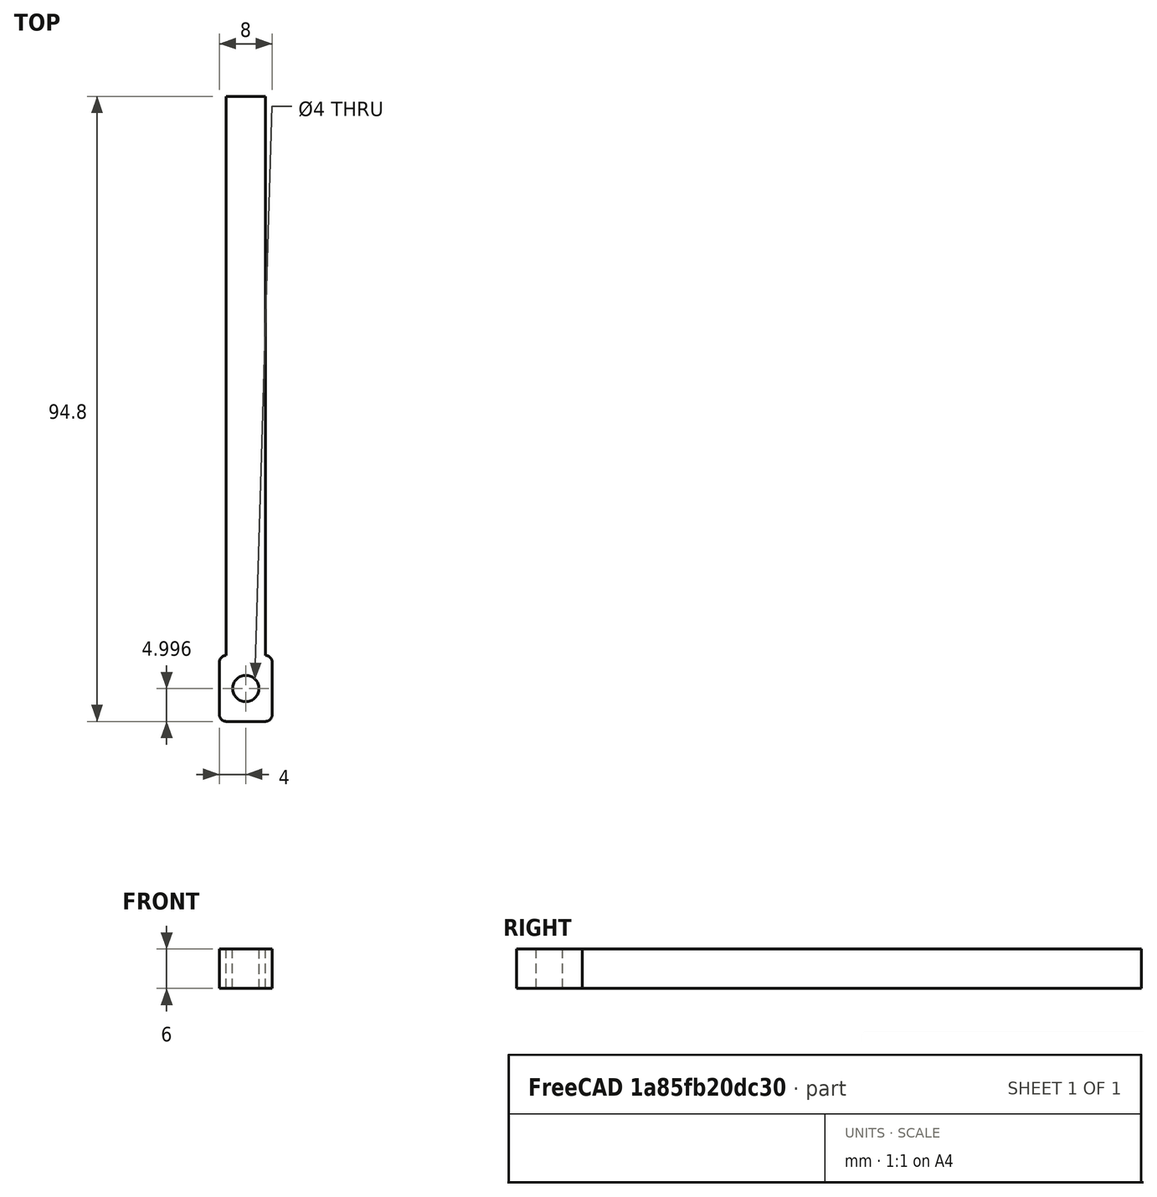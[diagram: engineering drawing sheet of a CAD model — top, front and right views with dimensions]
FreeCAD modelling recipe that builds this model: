
FCSTD DOCUMENT  (FreeCAD 0.18.1R)
Label: shub5R
License: All rights reserved
LicenseURL: http://en.wikipedia.org/wiki/All_rights_reserved
objects: TechDraw::DrawViewDimension×8, TechDraw::DrawProjGroupItem×4, Sketcher::SketchObject×3, PartDesign::Pocket×2, PartDesign::Pad×1, PartDesign::Body×1, TechDraw::DrawSVGTemplate×1, TechDraw::DrawProjGroup×1, TechDraw::DrawPage×1
note: 10 computed .brp shape members not serialized (recipe doc carries the construction recipe); baked Part::Feature solids carry a one-line shape summary decoded from their .brp

FEATURE [Sketcher::SketchObject] Sketch
  MapMode = 5
  Support = -> [XY_Plane]
  sketch-geometry (8):
    g0: LineSegment StartX=1 StartY=94.8 StartZ=0 EndX=7 EndY=94.8 EndZ=0
    g1: LineSegment StartX=7 StartY=94.8 StartZ=0 EndX=7 EndY=10 EndZ=0
    g2: LineSegment StartX=7 StartY=10 StartZ=0 EndX=8 EndY=10 EndZ=0
    g3: LineSegment StartX=8 StartY=10 StartZ=0 EndX=8 EndY=0 EndZ=0
    g4: LineSegment StartX=8 StartY=0 StartZ=0 EndX=0 EndY=0 EndZ=0
    g5: LineSegment StartX=0 StartY=0 StartZ=0 EndX=0 EndY=10 EndZ=0
    g6: LineSegment StartX=0 StartY=10 StartZ=0 EndX=1 EndY=10 EndZ=0
    g7: LineSegment StartX=1 StartY=10 StartZ=0 EndX=1 EndY=94.8 EndZ=0
  constraints (23):
    c: Coincident(g0,g1)
    c: Coincident(g1,g2)
    c: Coincident(g2,g3)
    c: Coincident(g3,g4)
    c: Coincident(g4,g5)
    c: Coincident(g5,g6)
    c: Coincident(g6,g7)
    c: Coincident(g7,g0)
    c: Vertical(g7)
    c: Horizontal(g0)
    c: DistanceY(g7,g7) = 84.8
    c: Horizontal(g6)
    c: DistanceY(g1,g1) = 84.8
    c: Horizontal(g2)
    c: Vertical(g1)
    c: DistanceX(g0,g0) = 6
    c: Vertical(g5)
    c: Vertical(g3)
    c: Horizontal(g4)
    c: DistanceY(g5,g5) = 10
    c: DistanceX(g4,g4) = 8
    c: DistanceX(g6,g6) = 1
    c: Coincident(g4,g-1)
FEATURE [PartDesign::Pad] Pad
  Length = 6
  Length2 = 100
  Profile = -> Sketch
  Type = 0
FEATURE [Sketcher::SketchObject] Sketch001
  ExternalGeometry = -> [Pad]
  MapMode = 5
  Placement = pos=(0,0,6) rot=(0,0,1;0rad)
  Support = -> [Pad]
  sketch-geometry (1):
    g0: Circle CenterX=4 CenterY=4.996 CenterZ=0 NormalX=0 NormalY=0 NormalZ=1 AngleXU=0 Radius=2
  constraints (3):
    c: Radius(g0) = 2
    c: Distance(g-1,g0) = 6.4
    c: Distance(g0,g-3) = 4
FEATURE [PartDesign::Pocket] Pocket
  BaseFeature = -> Pad
  Length = 8
  Length2 = 100
  Profile = -> Sketch001
  Type = 0
FEATURE [Sketcher::SketchObject] Sketch002
  ExternalGeometry = -> [Pocket]
  MapMode = 5
  Placement = pos=(0,0,6) rot=(0,0,1;0rad)
  Support = -> [Pocket]
  sketch-geometry (12):
    g0: ArcOfCircle CenterX=1 CenterY=1 CenterZ=0 NormalX=0 NormalY=0 NormalZ=1 AngleXU=0 Radius=1 StartAngle=3.14159 EndAngle=4.71239
    g1: ArcOfCircle CenterX=1 CenterY=9 CenterZ=0 NormalX=0 NormalY=0 NormalZ=1 AngleXU=0 Radius=1 StartAngle=1.5708 EndAngle=3.14159
    g2: ArcOfCircle CenterX=7 CenterY=9 CenterZ=0 NormalX=0 NormalY=0 NormalZ=1 AngleXU=0 Radius=1 StartAngle=1.3777e-12 EndAngle=1.5708
    g3: ArcOfCircle CenterX=7 CenterY=1 CenterZ=0 NormalX=0 NormalY=0 NormalZ=1 AngleXU=0 Radius=1 StartAngle=4.71239 EndAngle=6.28319
    g4: LineSegment StartX=0 StartY=9 StartZ=0 EndX=0 EndY=10 EndZ=0
    g5: LineSegment StartX=0 StartY=10 StartZ=0 EndX=1 EndY=10 EndZ=0
    g6: LineSegment StartX=0 StartY=1 StartZ=0 EndX=0 EndY=0 EndZ=0
    g7: LineSegment StartX=0 StartY=0 StartZ=0 EndX=1 EndY=0 EndZ=0
    g8: LineSegment StartX=7 StartY=0 StartZ=0 EndX=8 EndY=0 EndZ=0
    g9: LineSegment StartX=8 StartY=0 StartZ=0 EndX=8 EndY=1 EndZ=0
    g10: LineSegment StartX=7 StartY=10 StartZ=0 EndX=8 EndY=10 EndZ=0
    g11: LineSegment StartX=8 StartY=10 StartZ=0 EndX=8 EndY=9 EndZ=0
  constraints (37):
    c: Coincident(g1,g-5)
    c: Angle(g1) = 1.5708
    c: Angle(g2) = 1.5708
    c: Radius(g2) = 1
    c: Radius(g3) = 1
    c: Coincident(g4,g5)
    c: Coincident(g6,g7)
    c: Coincident(g8,g9)
    c: Coincident(g10,g11)
    c: Vertical(g4)
    c: Coincident(g4,g1)
    c: Coincident(g1,g5)
    c: Horizontal(g5)
    c: Radius(g1) = 1
    c: DistanceX(g5,g5) = 1
    c: Coincident(g0,g6)
    c: Coincident(g0,g7)
    c: Horizontal(g7)
    c: Vertical(g6)
    c: Radius(g0) = 1
    c: DistanceX(g7,g7) = 1
    c: Coincident(g6,g-1)
    c: Coincident(g9,g3)
    c: Coincident(g8,g-7)
    c: Angle(g3) = 1.5708
    c: DistanceY(g9,g9) = 1
    c: Coincident(g3,g8)
    c: Vertical(g9)
    c: Horizontal(g8)
    c: Coincident(g10,g-7)
    c: Vertical(g11)
    c: Horizontal(g10)
    c: DistanceY(g11,g11) = 1
    c: Distance(g2,g3) = 8
    c: Distance(g1,g0) = 8
    c: Distance(g1,g2) = 6
    c: Coincident(g2,g10)
FEATURE [PartDesign::Pocket] Pocket001
  BaseFeature = -> Pocket
  Length = 7
  Length2 = 100
  Profile = -> Sketch002
  Type = 0
FEATURE [PartDesign::Body] Body
  Group = -> [Sketch,Pad,Sketch001,Pocket,Sketch002,Pocket001]
  Origin = -> Origin
  Tip = -> Pocket001
FEATURE [TechDraw::DrawSVGTemplate] Template
  EditableTexts = Designed_by_Name=Designed by Name; Drawing_number=Drawing number; FC-Date=Date; FC-SC=Scale; FC-SH=Sheet; FC-Title=Title; Subtitle=Subtitle; Weight=Weight
  Height = 210
  Orientation = 1
  Width = 297
FEATURE [TechDraw::DrawProjGroupItem] ProjItem  label="Front"
  CoarseView = false
  Direction = (0,-1,0)
  Focus = 100
  HardHidden = false
  IsoCount = 0
  IsoHidden = false
  IsoVisible = false
  LockPosition = true
  Perspective = false
  Rotation = 0
  RotationVector = (1,0,0)
  ScaleType = 2
  SeamHidden = false
  SeamVisible = false
  SmoothHidden = false
  SmoothVisible = false
  Source = -> [Body]
  Type = 0
  X = 0
  Y = 0
FEATURE [TechDraw::DrawProjGroupItem] ProjItem001  label="Top"
  CoarseView = false
  Direction = (0,0,1)
  Focus = 100
  HardHidden = false
  IsoCount = 0
  IsoHidden = false
  IsoVisible = false
  LockPosition = false
  Perspective = false
  Rotation = 0
  RotationVector = (1,0,0)
  ScaleType = 2
  SeamHidden = false
  SeamVisible = false
  SmoothHidden = false
  SmoothVisible = false
  Source = -> [Body]
  Type = 4
  X = 0
  Y = -83.8297
FEATURE [TechDraw::DrawProjGroupItem] ProjItem002  label="FrontTopLeft"
  CoarseView = false
  Direction = (-1,-1,1)
  Focus = 100
  HardHidden = false
  IsoCount = 0
  IsoHidden = false
  IsoVisible = false
  LockPosition = false
  Perspective = false
  Rotation = 0
  RotationVector = (1,-1,0)
  ScaleType = 2
  SeamHidden = false
  SeamVisible = false
  SmoothHidden = false
  SmoothVisible = false
  Source = -> [Body]
  Type = 6
  X = 102.875
  Y = -74.1341
FEATURE [TechDraw::DrawProjGroupItem] ProjItem003  label="Left"
  CoarseView = false
  Direction = (-1,-1e-16,0)
  Focus = 100
  HardHidden = false
  IsoCount = 0
  IsoHidden = false
  IsoVisible = false
  LockPosition = false
  Perspective = false
  Rotation = 0
  RotationVector = (1e-16,-1,0)
  ScaleType = 2
  SeamHidden = false
  SeamVisible = false
  SmoothHidden = false
  SmoothVisible = false
  Source = -> [Body]
  Type = 1
  X = 109.8
  Y = 0
FEATURE [TechDraw::DrawProjGroup] ProjGroup
  Anchor = -> ProjItem
  AutoDistribute = true
  LockPosition = false
  ProjectionType = 1
  Rotation = 0
  ScaleType = 0
  Source = -> [Body]
  Views = -> [ProjItem,ProjItem001,ProjItem002,ProjItem003]
  X = 39.6326
  Y = 178.132
  spacingX = 15
  spacingY = 15
FEATURE [TechDraw::DrawViewDimension] Dimension
  Arbitrary = false
  FormatSpec = %.2f
  LockPosition = false
  MeasureType = 1
  OverTolerance = 0
  References2D = -> [ProjItem]
  Rotation = 0
  ScaleType = 0
  Type = 2
  UnderTolerance = 0
  X = 22.4392
  Y = -13.1708
FEATURE [TechDraw::DrawViewDimension] Dimension001
  Arbitrary = false
  FormatSpec = %.2f
  LockPosition = false
  MeasureType = 1
  OverTolerance = 0
  References2D = -> [ProjItem]
  Rotation = 0
  ScaleType = 0
  Type = 1
  UnderTolerance = 0
  X = 0.526834
  Y = 16.4343
FEATURE [TechDraw::DrawViewDimension] Dimension002
  Arbitrary = false
  FormatSpec = %.2f
  LockPosition = false
  MeasureType = 1
  OverTolerance = 0
  References2D = -> [ProjItem003]
  Rotation = 0
  ScaleType = 0
  Type = 1
  UnderTolerance = 0
  X = -6.13796
  Y = 12.483
FEATURE [TechDraw::DrawViewDimension] Dimension003
  Arbitrary = false
  FormatSpec = %.2f
  LockPosition = false
  MeasureType = 1
  OverTolerance = 0
  References2D = -> [ProjItem003]
  Rotation = 0
  ScaleType = 0
  Type = 2
  UnderTolerance = 0
  X = -66.366
  Y = -2.27592
FEATURE [TechDraw::DrawViewDimension] Dimension004
  Arbitrary = false
  FormatSpec = %.2f
  LockPosition = false
  MeasureType = 1
  OverTolerance = 0
  References2D = -> [ProjItem001]
  Rotation = 0
  ScaleType = 0
  Type = 2
  UnderTolerance = 0
  X = 19.3108
  Y = -1.44844
FEATURE [TechDraw::DrawViewDimension] Dimension005
  Arbitrary = false
  FormatSpec = %.2f
  LockPosition = false
  MeasureType = 1
  OverTolerance = 0
  References2D = -> [ProjItem001]
  Rotation = 0
  ScaleType = 0
  Type = 1
  UnderTolerance = 0
  X = -12.0733
  Y = 57.7172
FEATURE [TechDraw::DrawViewDimension] Dimension006
  Arbitrary = false
  FormatSpec = ⌀%.2f
  LockPosition = false
  MeasureType = 1
  OverTolerance = 0
  References2D = -> [ProjItem001]
  Rotation = 0
  ScaleType = 0
  Type = 5
  UnderTolerance = 0
  X = 25.2224
  Y = -51.7978
FEATURE [TechDraw::DrawViewDimension] Dimension007
  Arbitrary = false
  FormatSpec = R%.2f
  LockPosition = false
  MeasureType = 1
  OverTolerance = 0
  References2D = -> [ProjItem001]
  Rotation = 0
  ScaleType = 0
  Type = 4
  UnderTolerance = 0
  X = 36.0121
  Y = -74.4481
FEATURE [TechDraw::DrawPage] Page
  KeepUpdated = true
  ProjectionType = 0
  Template = -> Template
  Views = -> [ProjGroup,Dimension,Dimension001,Dimension002,Dimension003,Dimension004,Dimension005,Dimension006,Dimension007]
